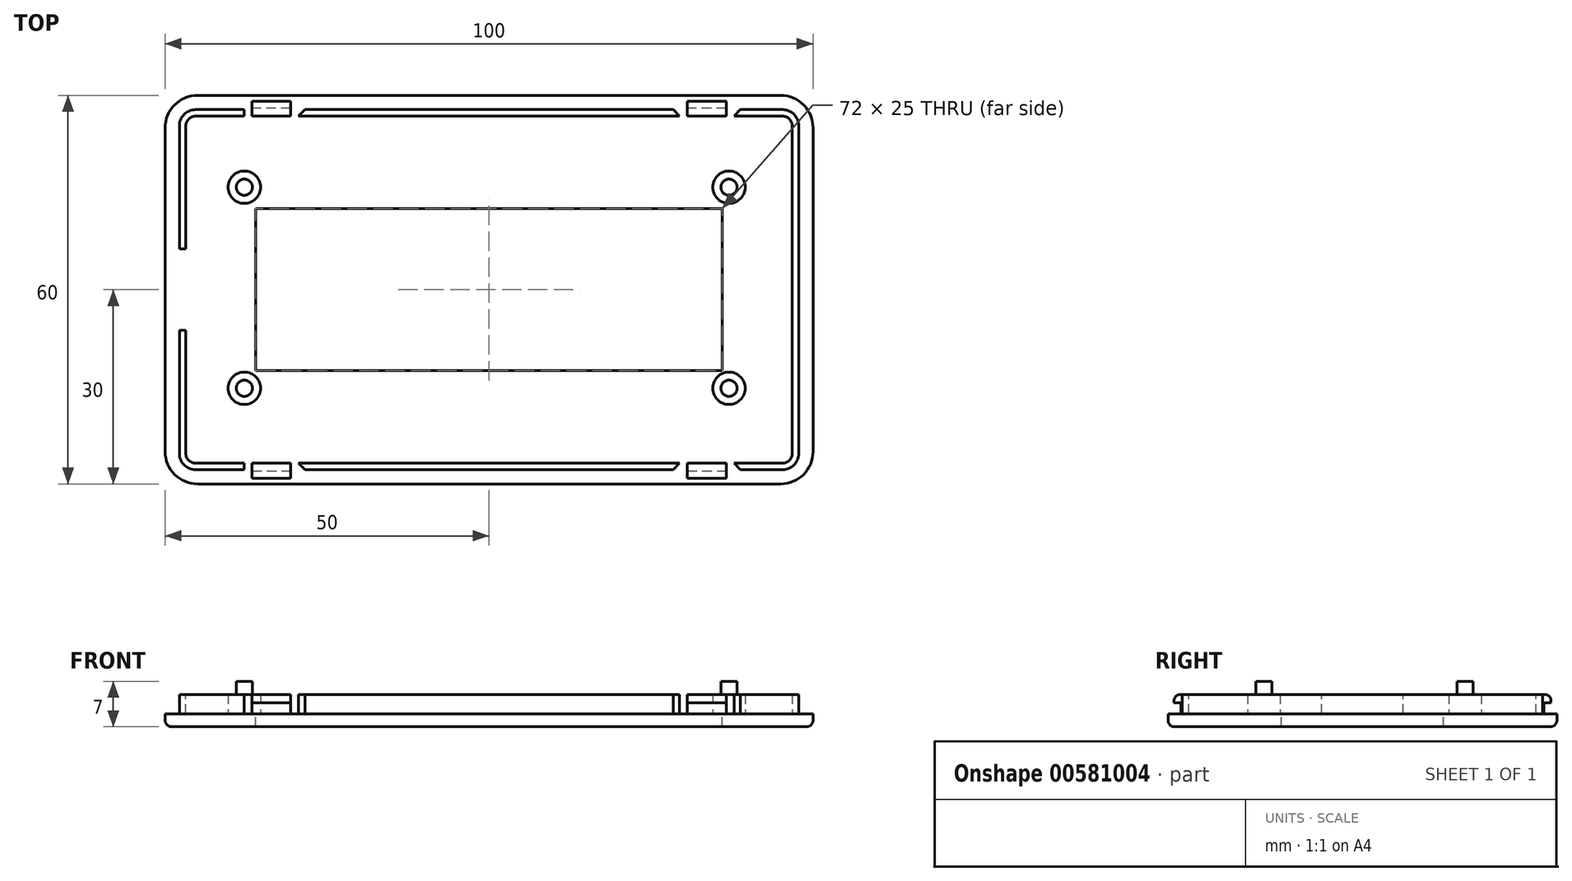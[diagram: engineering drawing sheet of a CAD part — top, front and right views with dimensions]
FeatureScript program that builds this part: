
annotation { "Feature Type Name" : "Feature", "Feature Type Description" : "" }
export const myFeature = defineFeature(function(context is Context, id is Id, definition is map)
    precondition{}
    {
        {
            var Q0;
            Q0=qCreatedBy(makeId("Top.planeOp"),FACE);
            var sketch = newSketch(context, id + "F0", { "sketchPlane" : qUnion([Q0])});
            skLineSegment(sketch, "E0.bottom", {"start": v(5, 0) * mm, "end": v(95, 0) * mm});
            skLineSegment(sketch, "E0.left", {"start": v(0, 5) * mm, "end": v(0, 30) * mm});
            skLineSegment(sketch, "E0.right", {"start": v(100, 5) * mm, "end": v(100, 30) * mm});
            skLineSegment(sketch, "E1.top", {"start": v(4.7, 2.2) * mm, "end": v(95.3, 2.2) * mm});
            skLineSegment(sketch, "E1.left", {"start": v(2.2, 30) * mm, "end": v(2.2, 4.7) * mm});
            skLineSegment(sketch, "E1.right", {"start": v(97.8, 30) * mm, "end": v(97.8, 4.7) * mm});
            skPoint(sketch, "E2.visualSharp", {"position": v(0, 0) * mm});
            skArc(sketch, "E2.filletArc", {"start": v(0, 5) * mm, "mid": v(1.46, 1.46) * mm, "end": v(5, 0) * mm});
            skPoint(sketch, "E3.visualSharp", {"position": v(100, 0) * mm});
            skArc(sketch, "E3.filletArc", {"start": v(95, 0) * mm, "mid": v(98.54, 1.46) * mm, "end": v(100, 5) * mm});
            skPoint(sketch, "E4.visualSharp", {"position": v(97.8, 2.2) * mm});
            skArc(sketch, "E4.filletArc", {"start": v(95.3, 2.2) * mm, "mid": v(97.07, 2.93) * mm, "end": v(97.8, 4.7) * mm});
            skPoint(sketch, "E5.visualSharp", {"position": v(2.2, 2.2) * mm});
            skArc(sketch, "E5.filletArc", {"start": v(2.2, 4.7) * mm, "mid": v(2.93, 2.93) * mm, "end": v(4.7, 2.2) * mm});
            skLineSegment(sketch, "E6.1", {"start": v(3.2, 30) * mm, "end": v(3.2, 4.7) * mm});
            skLineSegment(sketch, "E6.2", {"start": v(4.7, 3.2) * mm, "end": v(95.3, 3.2) * mm});
            skLineSegment(sketch, "E6.3", {"start": v(96.8, 30) * mm, "end": v(96.8, 4.7) * mm});
            skPoint(sketch, "E7.visualSharp", {"position": v(96.8, 3.2) * mm});
            skArc(sketch, "E7.filletArc", {"start": v(95.3, 3.2) * mm, "mid": v(96.36, 3.64) * mm, "end": v(96.8, 4.7) * mm});
            skPoint(sketch, "E8.visualSharp", {"position": v(3.2, 3.2) * mm});
            skArc(sketch, "E8.filletArc", {"start": v(3.2, 4.7) * mm, "mid": v(3.64, 3.64) * mm, "end": v(4.7, 3.2) * mm});
            skLineSegment(sketch, "E9", {"start": v(0, 30) * mm, "end": v(100, 30) * mm});
            skSolve(sketch);
        }
        {
            var Q0;
            Q0=qSketchRegion(id+"F0",true);
            var Q1;
            Q1=makeQuery(id+"F0.imprint","IMPRINT",FACE,{"disambiguationData":[TD([[makeQuery(id+"F0.imprint","IMPRINT",EDGE,{"derivedFrom":sQuery(id+"F0.wireOp",EDGE,"E6.0")}),-1.0]])]});
            var Q2;
            Q2=makeQuery(id+"F0.imprint","IMPRINT",FACE,{"disambiguationData":[TD([[makeQuery(id+"F0.imprint","IMPRINT",EDGE,{"derivedFrom":sQuery(id+"F0.wireOp",EDGE,"E1.bottom")}),-1.0]])]});
            extrude(context, id + "F1", {"entities" : qUnion([Q0, Q1, Q2]), "depth" : 2 * mm, "offsetDistance" : 25 * mm});
        }
        {
            var Q0;
            Q0=makeQuery(id+"F0.imprint","IMPRINT",FACE,{"disambiguationData":[TD([[makeQuery(id+"F0.imprint","IMPRINT",EDGE,{"derivedFrom":sQuery(id+"F0.wireOp",EDGE,"E1.top")}),1.0]])]});
            extrude(context, id + "F2", {"entities" : qUnion([Q0]), "operationType" : NewBodyOperationType.ADD, "depth" : 5 * mm, "offsetDistance" : 25 * mm});
        }
        {
            var Q0;
            Q0=makeQuery(id+"F2.opExtrude","CAP_FACE",FACE,{"disambiguationData":[OSD([sQuery(id+"F0.wireOp",EDGE,"E1.top"),sQuery(id+"F0.wireOp",EDGE,"E1.left"),sQuery(id+"F0.wireOp",EDGE,"E1.right"),sQuery(id+"F0.wireOp",EDGE,"E4.filletArc"),sQuery(id+"F0.wireOp",EDGE,"E5.filletArc"),sQuery(id+"F0.wireOp",EDGE,"E6.1"),sQuery(id+"F0.wireOp",EDGE,"E6.2"),sQuery(id+"F0.wireOp",EDGE,"E6.3"),sQuery(id+"F0.wireOp",EDGE,"E7.filletArc"),sQuery(id+"F0.wireOp",EDGE,"E8.filletArc"),sQuery(id+"F0.wireOp",EDGE,"E9")])],"isStart":false});
            var sketch = newSketch(context, id + "F3", { "sketchPlane" : qUnion([Q0])});
            skLineSegment(sketch, "E10.bottom", {"start": v(2.2, 30) * mm, "end": v(3.2, 30) * mm});
            skLineSegment(sketch, "E10.top", {"start": v(2.2, 23.7) * mm, "end": v(3.2, 23.7) * mm});
            skLineSegment(sketch, "E10.left", {"start": v(2.2, 30) * mm, "end": v(2.2, 23.7) * mm});
            skLineSegment(sketch, "E10.right", {"start": v(3.2, 30) * mm, "end": v(3.2, 23.7) * mm});
            skLineSegment(sketch, "E11.bottom", {"start": v(12.2, 3.2) * mm, "end": v(13.4, 3.2) * mm});
            skLineSegment(sketch, "E11.top", {"start": v(12.2, 2.2) * mm, "end": v(13.4, 2.2) * mm});
            skLineSegment(sketch, "E11.left", {"start": v(12.2, 3.2) * mm, "end": v(12.2, 2.2) * mm});
            skLineSegment(sketch, "E11.right", {"start": v(13.4, 3.2) * mm, "end": v(13.4, 2.2) * mm});
            skLineSegment(sketch, "E12.bottom", {"start": v(86.6, 3.2) * mm, "end": v(87.8, 3.2) * mm});
            skLineSegment(sketch, "E12.top", {"start": v(86.6, 2.2) * mm, "end": v(87.8, 2.2) * mm});
            skLineSegment(sketch, "E12.left", {"start": v(86.6, 3.2) * mm, "end": v(86.6, 2.2) * mm});
            skLineSegment(sketch, "E12.right", {"start": v(87.8, 3.2) * mm, "end": v(87.8, 2.2) * mm});
            skLineSegment(sketch, "E13.bottom", {"start": v(19.4, 3.2) * mm, "end": v(20.6, 3.2) * mm});
            skLineSegment(sketch, "E13.top", {"start": v(19.4, 2.2) * mm, "end": v(20.6, 2.2) * mm});
            skLineSegment(sketch, "E13.left", {"start": v(19.4, 3.2) * mm, "end": v(19.4, 2.2) * mm});
            skLineSegment(sketch, "E13.right", {"start": v(20.6, 3.2) * mm, "end": v(20.6, 2.2) * mm});
            skLineSegment(sketch, "E14.bottom", {"start": v(80.6, 3.2) * mm, "end": v(79.4, 3.2) * mm});
            skLineSegment(sketch, "E14.top", {"start": v(80.6, 2.2) * mm, "end": v(79.4, 2.2) * mm});
            skLineSegment(sketch, "E14.left", {"start": v(80.6, 3.2) * mm, "end": v(80.6, 2.2) * mm});
            skLineSegment(sketch, "E14.right", {"start": v(79.4, 3.2) * mm, "end": v(79.4, 2.2) * mm});
            skSolve(sketch);
        }
        {
            var Q0;
            Q0=makeQuery(id+"F3.imprint","IMPRINT",FACE,{"disambiguationData":[TD([[makeQuery(id+"F3.imprint","IMPRINT",EDGE,{"derivedFrom":sQuery(id+"F3.wireOp",EDGE,"E10.bottom")}),-1.0]])]});
            var Q1;
            Q1=makeQuery(id+"F3.imprint","IMPRINT",FACE,{"disambiguationData":[TD([[makeQuery(id+"F3.imprint","IMPRINT",EDGE,{"derivedFrom":sQuery(id+"F3.wireOp",EDGE,"E11.bottom")}),-1.0]])]});
            var Q2;
            Q2=makeQuery(id+"F3.imprint","IMPRINT",FACE,{"disambiguationData":[TD([[makeQuery(id+"F3.imprint","IMPRINT",EDGE,{"derivedFrom":sQuery(id+"F3.wireOp",EDGE,"E13.bottom")}),-1.0]])]});
            var Q3;
            Q3=makeQuery(id+"F3.imprint","IMPRINT",FACE,{"disambiguationData":[TD([[makeQuery(id+"F3.imprint","IMPRINT",EDGE,{"derivedFrom":sQuery(id+"F3.wireOp",EDGE,"E14.bottom")}),-1.0]])]});
            var Q4;
            Q4=makeQuery(id+"F3.imprint","IMPRINT",FACE,{"disambiguationData":[TD([[makeQuery(id+"F3.imprint","IMPRINT",EDGE,{"derivedFrom":sQuery(id+"F3.wireOp",EDGE,"E12.bottom")}),-1.0]])]});
            extrude(context, id + "F4", {"entities" : qUnion([Q0, Q1, Q2, Q3, Q4]), "operationType" : NewBodyOperationType.REMOVE, "oppositeDirection" : true, "depth" : 3 * mm, "offsetDistance" : 25 * mm});
        }
        {
            var Q0;
            {var subQ0=sQuery(id+"F3.wireOp",EDGE,"E11.right");var subQ2=sQuery(id+"F0.wireOp",EDGE,"E1.top");Q0=makeQuery(id+"F4.boolean.opBoolean","SPLIT",FACE,{"disambiguationData":[TD([makeQuery(id+"F4.opExtrude","SWEPT_FACE",FACE,{"disambiguationData":[OSD([subQ0])]})])],"derivedFrom":makeQuery(id+"F2.opExtrude","SWEPT_FACE",FACE,{"disambiguationData":[OSD([subQ2])]})});}
            var Q1;
            {var subQ1=sQuery(id+"F0.wireOp",EDGE,"E1.top");var subQ3=sQuery(id+"F3.wireOp",EDGE,"E12.left");Q1=makeQuery(id+"F4.boolean.opBoolean","SPLIT",FACE,{"disambiguationData":[TD([makeQuery(id+"F4.opExtrude","SWEPT_FACE",FACE,{"disambiguationData":[OSD([subQ3])]})])],"derivedFrom":makeQuery(id+"F2.opExtrude","SWEPT_FACE",FACE,{"disambiguationData":[OSD([subQ1])]})});}
            extrude(context, id + "F5", {"entities" : qUnion([Q0, Q1]), "operationType" : NewBodyOperationType.ADD, "depth" : 0.2 * mm, "offsetDistance" : 25 * mm});
        }
        {
            var Q0;
            {var subQ0=sQuery(id+"F3.wireOp",EDGE,"E11.right");var subQ2=sQuery(id+"F0.wireOp",EDGE,"E1.top");Q0=makeQuery(id+"F5.opExtrude","CAP_FACE",FACE,{"disambiguationData":[OSD([subQ2]),TDD([makeQuery(id+"F4.boolean.opBoolean","SPLIT",FACE,{"disambiguationData":[TD([makeQuery(id+"F4.opExtrude","SWEPT_FACE",FACE,{"disambiguationData":[OSD([subQ0])]})])],"derivedFrom":makeQuery(id+"F2.opExtrude","SWEPT_FACE",FACE,{"disambiguationData":[OSD([subQ2])]})})])],"isStart":false});}
            var sketch = newSketch(context, id + "F6", { "sketchPlane" : qUnion([Q0])});
            skLineSegment(sketch, "E15.bottom", {"start": v(13.4, 5) * mm, "end": v(19.4, 5) * mm});
            skLineSegment(sketch, "E15.top", {"start": v(13.4, 3.7) * mm, "end": v(19.4, 3.7) * mm});
            skLineSegment(sketch, "E15.left", {"start": v(13.4, 5) * mm, "end": v(13.4, 3.7) * mm});
            skLineSegment(sketch, "E15.right", {"start": v(19.4, 5) * mm, "end": v(19.4, 3.7) * mm});
            skSolve(sketch);
        }
        {
            var Q0;
            {var subQ1=sQuery(id+"F0.wireOp",EDGE,"E1.top");var subQ3=sQuery(id+"F3.wireOp",EDGE,"E12.left");Q0=makeQuery(id+"F5.opExtrude","CAP_FACE",FACE,{"disambiguationData":[OSD([subQ1]),TDD([makeQuery(id+"F4.boolean.opBoolean","SPLIT",FACE,{"disambiguationData":[TD([makeQuery(id+"F4.opExtrude","SWEPT_FACE",FACE,{"disambiguationData":[OSD([subQ3])]})])],"derivedFrom":makeQuery(id+"F2.opExtrude","SWEPT_FACE",FACE,{"disambiguationData":[OSD([subQ1])]})})])],"isStart":false});}
            var sketch = newSketch(context, id + "F7", { "sketchPlane" : qUnion([Q0])});
            skLineSegment(sketch, "E16.bottom", {"start": v(80.6, 5) * mm, "end": v(86.6, 5) * mm});
            skLineSegment(sketch, "E16.top", {"start": v(80.6, 3.7) * mm, "end": v(86.6, 3.7) * mm});
            skLineSegment(sketch, "E16.left", {"start": v(80.6, 5) * mm, "end": v(80.6, 3.7) * mm});
            skLineSegment(sketch, "E16.right", {"start": v(86.6, 5) * mm, "end": v(86.6, 3.7) * mm});
            skSolve(sketch);
        }
        {
            var Q0;
            Q0=makeQuery(id+"F6.imprint","IMPRINT",FACE,{"disambiguationData":[TD([[makeQuery(id+"F6.imprint","IMPRINT",EDGE,{"derivedFrom":sQuery(id+"F6.wireOp",EDGE,"E15.bottom")}),-1.0]])]});
            var Q1;
            Q1=makeQuery(id+"F7.imprint","IMPRINT",FACE,{"disambiguationData":[TD([[makeQuery(id+"F7.imprint","IMPRINT",EDGE,{"derivedFrom":sQuery(id+"F7.wireOp",EDGE,"E16.bottom")}),-1.0]])]});
            extrude(context, id + "F8", {"entities" : qUnion([Q0, Q1]), "operationType" : NewBodyOperationType.ADD, "depth" : 1.1 * mm, "offsetDistance" : 25 * mm});
        }
        {
            var Q0;
            Q0=makeQuery(id+"F8.opExtrude","CAP_EDGE",EDGE,{"disambiguationData":[OSD([sQuery(id+"F6.wireOp",EDGE,"E15.bottom")])],"isStart":false});
            var Q1;
            Q1=makeQuery(id+"F8.opExtrude","CAP_EDGE",EDGE,{"disambiguationData":[OSD([sQuery(id+"F7.wireOp",EDGE,"E16.bottom")])],"isStart":false});
            fillet(context, id + "F9", {"entities" : qUnion([Q0, Q1]), "radius" : 1 * mm, "tangentPropagation" : true, "allowEdgeOverflow" : false});
        }
        {
            var Q0;
            Q0=makeQuery(id+"F4.boolean.opBoolean","COPY",EDGE,{"derivedFrom":makeQuery(id+"F4.opExtrude","SWEPT_EDGE",EDGE,{"disambiguationData":[OSD([sQuery(id+"F0.wireOp",EDGE,"E1.top"),sQuery(id+"F3.wireOp",EDGE,"E13.top"),sQuery(id+"F3.wireOp",EDGE,"E13.right")])]})});
            var Q1;
            Q1=makeQuery(id+"F4.boolean.opBoolean","COPY",EDGE,{"derivedFrom":makeQuery(id+"F4.opExtrude","SWEPT_EDGE",EDGE,{"disambiguationData":[OSD([sQuery(id+"F0.wireOp",EDGE,"E1.top"),sQuery(id+"F3.wireOp",EDGE,"E11.top"),sQuery(id+"F3.wireOp",EDGE,"E11.left")])]})});
            var Q2;
            Q2=makeQuery(id+"F4.boolean.opBoolean","COPY",EDGE,{"derivedFrom":makeQuery(id+"F4.opExtrude","SWEPT_EDGE",EDGE,{"disambiguationData":[OSD([sQuery(id+"F0.wireOp",EDGE,"E1.top"),sQuery(id+"F3.wireOp",EDGE,"E14.top"),sQuery(id+"F3.wireOp",EDGE,"E14.right")])]})});
            var Q3;
            Q3=makeQuery(id+"F4.boolean.opBoolean","COPY",EDGE,{"derivedFrom":makeQuery(id+"F4.opExtrude","SWEPT_EDGE",EDGE,{"disambiguationData":[OSD([sQuery(id+"F0.wireOp",EDGE,"E1.top"),sQuery(id+"F3.wireOp",EDGE,"E12.top"),sQuery(id+"F3.wireOp",EDGE,"E12.right")])]})});
            var Q4;
            Q4=makeQuery(id+"F4.boolean.opBoolean","COPY",EDGE,{"derivedFrom":makeQuery(id+"F4.opExtrude","SWEPT_EDGE",EDGE,{"disambiguationData":[OSD([sQuery(id+"F0.wireOp",EDGE,"E1.left"),sQuery(id+"F3.wireOp",EDGE,"E10.top"),sQuery(id+"F3.wireOp",EDGE,"E10.left")])]})});
            chamfer(context, id + "F10", {"entities" : qUnion([Q0, Q1, Q2, Q3, Q4]), "width" : 1 * mm, "tangentPropagation" : true});
        }
        {
            var Q0;
            {var subQ2=sQuery(id+"F0.wireOp",EDGE,"E9");var subQ4=sQuery(id+"F0.wireOp",EDGE,"E3.filletArc");var subQ5=sQuery(id+"F0.wireOp",EDGE,"E0.bottom");var subQ6=sQuery(id+"F0.wireOp",EDGE,"E2.filletArc");var subQ7=sQuery(id+"F0.wireOp",EDGE,"E0.left");var subQ8=sQuery(id+"F0.wireOp",EDGE,"E0.right");var subQ9=sQuery(id+"F0.wireOp",EDGE,"E6.1");var subQ13=makeQuery(id+"F1.opExtrude","CAP_FACE",FACE,{"disambiguationData":[OSD([subQ5,subQ7,subQ8,subQ6,subQ4,subQ2])],"isStart":false});Q0=makeQuery(id+"F4.boolean.opBoolean","MERGE",FACE,{"derivedFrom":[makeQuery(id+"F2.boolean.opBoolean","SPLIT",FACE,{"disambiguationData":[TD([makeQuery(id+"F2.opExtrude","SWEPT_FACE",FACE,{"disambiguationData":[OSD([subQ9])]})])],"derivedFrom":subQ13}),makeQuery(id+"F2.boolean.opBoolean","SPLIT",FACE,{"disambiguationData":[TD([makeQuery(id+"F1.opExtrude","SWEPT_FACE",FACE,{"disambiguationData":[OSD([subQ5])]})])],"derivedFrom":subQ13}),makeQuery(id+"F4.opExtrude","CAP_FACE",FACE,{"disambiguationData":[OSD([sQuery(id+"F3.wireOp",EDGE,"E10.bottom"),sQuery(id+"F3.wireOp",EDGE,"E10.top"),sQuery(id+"F3.wireOp",EDGE,"E10.left"),sQuery(id+"F3.wireOp",EDGE,"E10.right")])],"isStart":false}),makeQuery(id+"F4.opExtrude","CAP_FACE",FACE,{"disambiguationData":[OSD([sQuery(id+"F3.wireOp",EDGE,"E11.bottom"),sQuery(id+"F3.wireOp",EDGE,"E11.top"),sQuery(id+"F3.wireOp",EDGE,"E11.left"),sQuery(id+"F3.wireOp",EDGE,"E11.right")])],"isStart":false}),makeQuery(id+"F4.opExtrude","CAP_FACE",FACE,{"disambiguationData":[OSD([sQuery(id+"F3.wireOp",EDGE,"E12.bottom"),sQuery(id+"F3.wireOp",EDGE,"E12.top"),sQuery(id+"F3.wireOp",EDGE,"E12.left"),sQuery(id+"F3.wireOp",EDGE,"E12.right")])],"isStart":false}),makeQuery(id+"F4.opExtrude","CAP_FACE",FACE,{"disambiguationData":[OSD([sQuery(id+"F3.wireOp",EDGE,"E13.bottom"),sQuery(id+"F3.wireOp",EDGE,"E13.top"),sQuery(id+"F3.wireOp",EDGE,"E13.left"),sQuery(id+"F3.wireOp",EDGE,"E13.right")])],"isStart":false}),makeQuery(id+"F4.opExtrude","CAP_FACE",FACE,{"disambiguationData":[OSD([sQuery(id+"F3.wireOp",EDGE,"E14.bottom"),sQuery(id+"F3.wireOp",EDGE,"E14.top"),sQuery(id+"F3.wireOp",EDGE,"E14.left"),sQuery(id+"F3.wireOp",EDGE,"E14.right")])],"isStart":false})]});}
            var sketch = newSketch(context, id + "F11", { "sketchPlane" : qUnion([Q0])});
            skLineSegment(sketch, "E17.bottom", {"start": v(86, 17.5) * mm, "end": v(14, 17.5) * mm});
            skLineSegment(sketch, "E17.top", {"start": v(86, 42.5) * mm, "end": v(14, 42.5) * mm});
            skLineSegment(sketch, "E17.left", {"start": v(86, 17.5) * mm, "end": v(86, 42.5) * mm});
            skLineSegment(sketch, "E17.right", {"start": v(14, 17.5) * mm, "end": v(14, 42.5) * mm});
            skPoint(sketch, "E17.middle", {"position": v(50, 30) * mm});
            skSolve(sketch);
        }
        {
            var Q0;
            {var subQ0=sQuery(id+"F11.wireOp",EDGE,"E17.bottom");Q0=makeQuery(id+"F11.imprint","IMPRINT",FACE,{"disambiguationData":[TD([[makeQuery(id+"F11.imprint","IMPRINT",EDGE,{"derivedFrom":subQ0}),-1.0]])]});}
            extrude(context, id + "F12", {"entities" : qUnion([Q0]), "operationType" : NewBodyOperationType.REMOVE, "endBound" : BoundingType.UP_TO_NEXT, "oppositeDirection" : true, "depth" : 25 * mm, "offsetDistance" : 25 * mm});
        }
        {
            var Q0;
            Q0=makeQuery(id+"F1.opExtrude","CAP_EDGE",EDGE,{"disambiguationData":[OSD([sQuery(id+"F0.wireOp",EDGE,"E0.bottom")])],"isStart":true});
            fillet(context, id + "F13", {"entities" : qUnion([Q0]), "radius" : 1 * mm, "tangentPropagation" : true, "allowEdgeOverflow" : false});
        }
        {
            var Q0;
            Q0=makeQuery(id+"F1.opExtrude","SWEPT_BODY",BODY,{"disambiguationData":[OSD([sQuery(id+"F0.wireOp",EDGE,"E0.bottom"),sQuery(id+"F0.wireOp",EDGE,"E0.left"),sQuery(id+"F0.wireOp",EDGE,"E0.right"),sQuery(id+"F0.wireOp",EDGE,"E2.filletArc"),sQuery(id+"F0.wireOp",EDGE,"E3.filletArc"),sQuery(id+"F0.wireOp",EDGE,"E9")])]});
            var Q1;
            {var subQ0=sQuery(id+"F0.wireOp",EDGE,"E0.left");var subQ1=sQuery(id+"F0.wireOp",EDGE,"E9");Q1=makeQuery(id+"F12.boolean.opBoolean","SPLIT",FACE,{"disambiguationData":[TD([makeQuery(id+"F1.opExtrude","SWEPT_FACE",FACE,{"disambiguationData":[OSD([subQ0])]})])],"derivedFrom":makeQuery(id+"F2.boolean.opBoolean","MERGE",FACE,{"derivedFrom":[makeQuery(id+"F1.opExtrude","SWEPT_FACE",FACE,{"disambiguationData":[OSD([subQ1])]}),makeQuery(id+"F2.opExtrude","SWEPT_FACE",FACE,{"disambiguationData":[OSD([subQ1]),TDD([makeQuery(id+"F0.imprint","IMPRINT",EDGE,{"disambiguationData":[TD([[makeQuery(id+"F0.imprint","INTERSECT",VERTEX,{"derivedFrom":[sQuery(id+"F0.wireOp",EDGE,"E1.left"),subQ1]}),-1.0]])],"derivedFrom":subQ1})])]}),makeQuery(id+"F2.opExtrude","SWEPT_FACE",FACE,{"disambiguationData":[OSD([subQ1]),TDD([makeQuery(id+"F0.imprint","IMPRINT",EDGE,{"disambiguationData":[TD([[makeQuery(id+"F0.imprint","INTERSECT",VERTEX,{"derivedFrom":[sQuery(id+"F0.wireOp",EDGE,"E1.right"),subQ1]}),1.0]])],"derivedFrom":subQ1})])]})]})});}
            mirror(context, id + "F14", {"operationType" : NewBodyOperationType.ADD, "entities" : qUnion([Q0]), "mirrorPlane" : qUnion([Q1])});
        }
        {
            var Q0;
            {var subQ2=sQuery(id+"F0.wireOp",EDGE,"E9");var subQ4=sQuery(id+"F0.wireOp",EDGE,"E3.filletArc");var subQ5=sQuery(id+"F0.wireOp",EDGE,"E0.bottom");var subQ6=sQuery(id+"F0.wireOp",EDGE,"E2.filletArc");var subQ7=sQuery(id+"F0.wireOp",EDGE,"E0.left");var subQ8=sQuery(id+"F0.wireOp",EDGE,"E0.right");var subQ9=sQuery(id+"F0.wireOp",EDGE,"E6.1");var subQ13=makeQuery(id+"F1.opExtrude","CAP_FACE",FACE,{"disambiguationData":[OSD([subQ5,subQ7,subQ8,subQ6,subQ4,subQ2])],"isStart":false});var subQ14=makeQuery(id+"F4.boolean.opBoolean","MERGE",FACE,{"derivedFrom":[makeQuery(id+"F2.boolean.opBoolean","SPLIT",FACE,{"disambiguationData":[TD([makeQuery(id+"F2.opExtrude","SWEPT_FACE",FACE,{"disambiguationData":[OSD([subQ9])]})])],"derivedFrom":subQ13}),makeQuery(id+"F2.boolean.opBoolean","SPLIT",FACE,{"disambiguationData":[TD([makeQuery(id+"F1.opExtrude","SWEPT_FACE",FACE,{"disambiguationData":[OSD([subQ5])]})])],"derivedFrom":subQ13}),makeQuery(id+"F4.opExtrude","CAP_FACE",FACE,{"disambiguationData":[OSD([sQuery(id+"F3.wireOp",EDGE,"E10.bottom"),sQuery(id+"F3.wireOp",EDGE,"E10.top"),sQuery(id+"F3.wireOp",EDGE,"E10.left"),sQuery(id+"F3.wireOp",EDGE,"E10.right")])],"isStart":false}),makeQuery(id+"F4.opExtrude","CAP_FACE",FACE,{"disambiguationData":[OSD([sQuery(id+"F3.wireOp",EDGE,"E11.bottom"),sQuery(id+"F3.wireOp",EDGE,"E11.top"),sQuery(id+"F3.wireOp",EDGE,"E11.left"),sQuery(id+"F3.wireOp",EDGE,"E11.right")])],"isStart":false}),makeQuery(id+"F4.opExtrude","CAP_FACE",FACE,{"disambiguationData":[OSD([sQuery(id+"F3.wireOp",EDGE,"E12.bottom"),sQuery(id+"F3.wireOp",EDGE,"E12.top"),sQuery(id+"F3.wireOp",EDGE,"E12.left"),sQuery(id+"F3.wireOp",EDGE,"E12.right")])],"isStart":false}),makeQuery(id+"F4.opExtrude","CAP_FACE",FACE,{"disambiguationData":[OSD([sQuery(id+"F3.wireOp",EDGE,"E13.bottom"),sQuery(id+"F3.wireOp",EDGE,"E13.top"),sQuery(id+"F3.wireOp",EDGE,"E13.left"),sQuery(id+"F3.wireOp",EDGE,"E13.right")])],"isStart":false}),makeQuery(id+"F4.opExtrude","CAP_FACE",FACE,{"disambiguationData":[OSD([sQuery(id+"F3.wireOp",EDGE,"E14.bottom"),sQuery(id+"F3.wireOp",EDGE,"E14.top"),sQuery(id+"F3.wireOp",EDGE,"E14.left"),sQuery(id+"F3.wireOp",EDGE,"E14.right")])],"isStart":false})]});Q0=makeQuery(id+"F14.boolean.opBoolean","MERGE",FACE,{"derivedFrom":[subQ14,makeQuery(id+"F14.opPattern","COPY",FACE,{"derivedFrom":subQ14,"instanceName":"1"})]});}
            var sketch = newSketch(context, id + "F15", { "sketchPlane" : qUnion([Q0])});
            skCircle(sketch, "E18", {"center": v(12.22, 45.83) * mm, "radius": 1.25 * mm});
            skCircle(sketch, "E19", {"center": v(87.03, 45.83) * mm, "radius": 1.25 * mm});
            skCircle(sketch, "E20", {"center": v(87.03, 14.78) * mm, "radius": 1.25 * mm});
            skCircle(sketch, "E21", {"center": v(12.22, 14.78) * mm, "radius": 1.25 * mm});
            skCircle(sketch, "E22", {"center": v(12.22, 45.83) * mm, "radius": 2.5 * mm});
            skCircle(sketch, "E23", {"center": v(87.03, 45.83) * mm, "radius": 2.5 * mm});
            skCircle(sketch, "E24", {"center": v(87.03, 14.78) * mm, "radius": 2.5 * mm});
            skCircle(sketch, "E25", {"center": v(12.22, 14.78) * mm, "radius": 2.5 * mm});
            skSolve(sketch);
        }
        {
            var Q0;
            Q0=qSketchRegion(id+"F15",true);
            extrude(context, id + "F16", {"entities" : qUnion([Q0]), "operationType" : NewBodyOperationType.ADD, "depth" : 3 * mm, "offsetDistance" : 25 * mm});
        }
        {
            var Q0;
            {var subQ2=sQuery(id+"F0.wireOp",EDGE,"E9");var subQ4=sQuery(id+"F0.wireOp",EDGE,"E3.filletArc");var subQ5=sQuery(id+"F0.wireOp",EDGE,"E0.bottom");var subQ6=sQuery(id+"F0.wireOp",EDGE,"E2.filletArc");var subQ7=sQuery(id+"F0.wireOp",EDGE,"E0.left");var subQ8=sQuery(id+"F0.wireOp",EDGE,"E0.right");var subQ9=sQuery(id+"F0.wireOp",EDGE,"E6.1");var subQ13=makeQuery(id+"F1.opExtrude","CAP_FACE",FACE,{"disambiguationData":[OSD([subQ5,subQ7,subQ8,subQ6,subQ4,subQ2])],"isStart":false});var subQ14=makeQuery(id+"F4.boolean.opBoolean","MERGE",FACE,{"derivedFrom":[makeQuery(id+"F2.boolean.opBoolean","SPLIT",FACE,{"disambiguationData":[TD([makeQuery(id+"F2.opExtrude","SWEPT_FACE",FACE,{"disambiguationData":[OSD([subQ9])]})])],"derivedFrom":subQ13}),makeQuery(id+"F2.boolean.opBoolean","SPLIT",FACE,{"disambiguationData":[TD([makeQuery(id+"F1.opExtrude","SWEPT_FACE",FACE,{"disambiguationData":[OSD([subQ5])]})])],"derivedFrom":subQ13}),makeQuery(id+"F4.opExtrude","CAP_FACE",FACE,{"disambiguationData":[OSD([sQuery(id+"F3.wireOp",EDGE,"E10.bottom"),sQuery(id+"F3.wireOp",EDGE,"E10.top"),sQuery(id+"F3.wireOp",EDGE,"E10.left"),sQuery(id+"F3.wireOp",EDGE,"E10.right")])],"isStart":false}),makeQuery(id+"F4.opExtrude","CAP_FACE",FACE,{"disambiguationData":[OSD([sQuery(id+"F3.wireOp",EDGE,"E11.bottom"),sQuery(id+"F3.wireOp",EDGE,"E11.top"),sQuery(id+"F3.wireOp",EDGE,"E11.left"),sQuery(id+"F3.wireOp",EDGE,"E11.right")])],"isStart":false}),makeQuery(id+"F4.opExtrude","CAP_FACE",FACE,{"disambiguationData":[OSD([sQuery(id+"F3.wireOp",EDGE,"E12.bottom"),sQuery(id+"F3.wireOp",EDGE,"E12.top"),sQuery(id+"F3.wireOp",EDGE,"E12.left"),sQuery(id+"F3.wireOp",EDGE,"E12.right")])],"isStart":false}),makeQuery(id+"F4.opExtrude","CAP_FACE",FACE,{"disambiguationData":[OSD([sQuery(id+"F3.wireOp",EDGE,"E13.bottom"),sQuery(id+"F3.wireOp",EDGE,"E13.top"),sQuery(id+"F3.wireOp",EDGE,"E13.left"),sQuery(id+"F3.wireOp",EDGE,"E13.right")])],"isStart":false}),makeQuery(id+"F4.opExtrude","CAP_FACE",FACE,{"disambiguationData":[OSD([sQuery(id+"F3.wireOp",EDGE,"E14.bottom"),sQuery(id+"F3.wireOp",EDGE,"E14.top"),sQuery(id+"F3.wireOp",EDGE,"E14.left"),sQuery(id+"F3.wireOp",EDGE,"E14.right")])],"isStart":false})]});Q0=makeQuery(id+"F16.boolean.opBoolean","SPLIT",FACE,{"disambiguationData":[TD([makeQuery(id+"F16.opExtrude","SWEPT_FACE",FACE,{"disambiguationData":[OSD([sQuery(id+"F15.wireOp",EDGE,"E21")])]})])],"derivedFrom":makeQuery(id+"F14.boolean.opBoolean","MERGE",FACE,{"derivedFrom":[subQ14,makeQuery(id+"F14.opPattern","COPY",FACE,{"derivedFrom":subQ14,"instanceName":"1"})]})});}
            var Q1;
            {var subQ2=sQuery(id+"F0.wireOp",EDGE,"E9");var subQ4=sQuery(id+"F0.wireOp",EDGE,"E3.filletArc");var subQ5=sQuery(id+"F0.wireOp",EDGE,"E0.bottom");var subQ6=sQuery(id+"F0.wireOp",EDGE,"E2.filletArc");var subQ7=sQuery(id+"F0.wireOp",EDGE,"E0.left");var subQ8=sQuery(id+"F0.wireOp",EDGE,"E0.right");var subQ9=sQuery(id+"F0.wireOp",EDGE,"E6.1");var subQ13=makeQuery(id+"F1.opExtrude","CAP_FACE",FACE,{"disambiguationData":[OSD([subQ5,subQ7,subQ8,subQ6,subQ4,subQ2])],"isStart":false});var subQ14=makeQuery(id+"F4.boolean.opBoolean","MERGE",FACE,{"derivedFrom":[makeQuery(id+"F2.boolean.opBoolean","SPLIT",FACE,{"disambiguationData":[TD([makeQuery(id+"F2.opExtrude","SWEPT_FACE",FACE,{"disambiguationData":[OSD([subQ9])]})])],"derivedFrom":subQ13}),makeQuery(id+"F2.boolean.opBoolean","SPLIT",FACE,{"disambiguationData":[TD([makeQuery(id+"F1.opExtrude","SWEPT_FACE",FACE,{"disambiguationData":[OSD([subQ5])]})])],"derivedFrom":subQ13}),makeQuery(id+"F4.opExtrude","CAP_FACE",FACE,{"disambiguationData":[OSD([sQuery(id+"F3.wireOp",EDGE,"E10.bottom"),sQuery(id+"F3.wireOp",EDGE,"E10.top"),sQuery(id+"F3.wireOp",EDGE,"E10.left"),sQuery(id+"F3.wireOp",EDGE,"E10.right")])],"isStart":false}),makeQuery(id+"F4.opExtrude","CAP_FACE",FACE,{"disambiguationData":[OSD([sQuery(id+"F3.wireOp",EDGE,"E11.bottom"),sQuery(id+"F3.wireOp",EDGE,"E11.top"),sQuery(id+"F3.wireOp",EDGE,"E11.left"),sQuery(id+"F3.wireOp",EDGE,"E11.right")])],"isStart":false}),makeQuery(id+"F4.opExtrude","CAP_FACE",FACE,{"disambiguationData":[OSD([sQuery(id+"F3.wireOp",EDGE,"E12.bottom"),sQuery(id+"F3.wireOp",EDGE,"E12.top"),sQuery(id+"F3.wireOp",EDGE,"E12.left"),sQuery(id+"F3.wireOp",EDGE,"E12.right")])],"isStart":false}),makeQuery(id+"F4.opExtrude","CAP_FACE",FACE,{"disambiguationData":[OSD([sQuery(id+"F3.wireOp",EDGE,"E13.bottom"),sQuery(id+"F3.wireOp",EDGE,"E13.top"),sQuery(id+"F3.wireOp",EDGE,"E13.left"),sQuery(id+"F3.wireOp",EDGE,"E13.right")])],"isStart":false}),makeQuery(id+"F4.opExtrude","CAP_FACE",FACE,{"disambiguationData":[OSD([sQuery(id+"F3.wireOp",EDGE,"E14.bottom"),sQuery(id+"F3.wireOp",EDGE,"E14.top"),sQuery(id+"F3.wireOp",EDGE,"E14.left"),sQuery(id+"F3.wireOp",EDGE,"E14.right")])],"isStart":false})]});Q1=makeQuery(id+"F16.boolean.opBoolean","SPLIT",FACE,{"disambiguationData":[TD([makeQuery(id+"F16.opExtrude","SWEPT_FACE",FACE,{"disambiguationData":[OSD([sQuery(id+"F15.wireOp",EDGE,"E18")])]})])],"derivedFrom":makeQuery(id+"F14.boolean.opBoolean","MERGE",FACE,{"derivedFrom":[subQ14,makeQuery(id+"F14.opPattern","COPY",FACE,{"derivedFrom":subQ14,"instanceName":"1"})]})});}
            var Q2;
            {var subQ2=sQuery(id+"F0.wireOp",EDGE,"E9");var subQ4=sQuery(id+"F0.wireOp",EDGE,"E3.filletArc");var subQ5=sQuery(id+"F0.wireOp",EDGE,"E0.bottom");var subQ6=sQuery(id+"F0.wireOp",EDGE,"E2.filletArc");var subQ7=sQuery(id+"F0.wireOp",EDGE,"E0.left");var subQ8=sQuery(id+"F0.wireOp",EDGE,"E0.right");var subQ9=sQuery(id+"F0.wireOp",EDGE,"E6.1");var subQ13=makeQuery(id+"F1.opExtrude","CAP_FACE",FACE,{"disambiguationData":[OSD([subQ5,subQ7,subQ8,subQ6,subQ4,subQ2])],"isStart":false});var subQ14=makeQuery(id+"F4.boolean.opBoolean","MERGE",FACE,{"derivedFrom":[makeQuery(id+"F2.boolean.opBoolean","SPLIT",FACE,{"disambiguationData":[TD([makeQuery(id+"F2.opExtrude","SWEPT_FACE",FACE,{"disambiguationData":[OSD([subQ9])]})])],"derivedFrom":subQ13}),makeQuery(id+"F2.boolean.opBoolean","SPLIT",FACE,{"disambiguationData":[TD([makeQuery(id+"F1.opExtrude","SWEPT_FACE",FACE,{"disambiguationData":[OSD([subQ5])]})])],"derivedFrom":subQ13}),makeQuery(id+"F4.opExtrude","CAP_FACE",FACE,{"disambiguationData":[OSD([sQuery(id+"F3.wireOp",EDGE,"E10.bottom"),sQuery(id+"F3.wireOp",EDGE,"E10.top"),sQuery(id+"F3.wireOp",EDGE,"E10.left"),sQuery(id+"F3.wireOp",EDGE,"E10.right")])],"isStart":false}),makeQuery(id+"F4.opExtrude","CAP_FACE",FACE,{"disambiguationData":[OSD([sQuery(id+"F3.wireOp",EDGE,"E11.bottom"),sQuery(id+"F3.wireOp",EDGE,"E11.top"),sQuery(id+"F3.wireOp",EDGE,"E11.left"),sQuery(id+"F3.wireOp",EDGE,"E11.right")])],"isStart":false}),makeQuery(id+"F4.opExtrude","CAP_FACE",FACE,{"disambiguationData":[OSD([sQuery(id+"F3.wireOp",EDGE,"E12.bottom"),sQuery(id+"F3.wireOp",EDGE,"E12.top"),sQuery(id+"F3.wireOp",EDGE,"E12.left"),sQuery(id+"F3.wireOp",EDGE,"E12.right")])],"isStart":false}),makeQuery(id+"F4.opExtrude","CAP_FACE",FACE,{"disambiguationData":[OSD([sQuery(id+"F3.wireOp",EDGE,"E13.bottom"),sQuery(id+"F3.wireOp",EDGE,"E13.top"),sQuery(id+"F3.wireOp",EDGE,"E13.left"),sQuery(id+"F3.wireOp",EDGE,"E13.right")])],"isStart":false}),makeQuery(id+"F4.opExtrude","CAP_FACE",FACE,{"disambiguationData":[OSD([sQuery(id+"F3.wireOp",EDGE,"E14.bottom"),sQuery(id+"F3.wireOp",EDGE,"E14.top"),sQuery(id+"F3.wireOp",EDGE,"E14.left"),sQuery(id+"F3.wireOp",EDGE,"E14.right")])],"isStart":false})]});Q2=makeQuery(id+"F16.boolean.opBoolean","SPLIT",FACE,{"disambiguationData":[TD([makeQuery(id+"F16.opExtrude","SWEPT_FACE",FACE,{"disambiguationData":[OSD([sQuery(id+"F15.wireOp",EDGE,"E19")])]})])],"derivedFrom":makeQuery(id+"F14.boolean.opBoolean","MERGE",FACE,{"derivedFrom":[subQ14,makeQuery(id+"F14.opPattern","COPY",FACE,{"derivedFrom":subQ14,"instanceName":"1"})]})});}
            var Q3;
            {var subQ2=sQuery(id+"F0.wireOp",EDGE,"E9");var subQ4=sQuery(id+"F0.wireOp",EDGE,"E3.filletArc");var subQ5=sQuery(id+"F0.wireOp",EDGE,"E0.bottom");var subQ6=sQuery(id+"F0.wireOp",EDGE,"E2.filletArc");var subQ7=sQuery(id+"F0.wireOp",EDGE,"E0.left");var subQ8=sQuery(id+"F0.wireOp",EDGE,"E0.right");var subQ9=sQuery(id+"F0.wireOp",EDGE,"E6.1");var subQ13=makeQuery(id+"F1.opExtrude","CAP_FACE",FACE,{"disambiguationData":[OSD([subQ5,subQ7,subQ8,subQ6,subQ4,subQ2])],"isStart":false});var subQ14=makeQuery(id+"F4.boolean.opBoolean","MERGE",FACE,{"derivedFrom":[makeQuery(id+"F2.boolean.opBoolean","SPLIT",FACE,{"disambiguationData":[TD([makeQuery(id+"F2.opExtrude","SWEPT_FACE",FACE,{"disambiguationData":[OSD([subQ9])]})])],"derivedFrom":subQ13}),makeQuery(id+"F2.boolean.opBoolean","SPLIT",FACE,{"disambiguationData":[TD([makeQuery(id+"F1.opExtrude","SWEPT_FACE",FACE,{"disambiguationData":[OSD([subQ5])]})])],"derivedFrom":subQ13}),makeQuery(id+"F4.opExtrude","CAP_FACE",FACE,{"disambiguationData":[OSD([sQuery(id+"F3.wireOp",EDGE,"E10.bottom"),sQuery(id+"F3.wireOp",EDGE,"E10.top"),sQuery(id+"F3.wireOp",EDGE,"E10.left"),sQuery(id+"F3.wireOp",EDGE,"E10.right")])],"isStart":false}),makeQuery(id+"F4.opExtrude","CAP_FACE",FACE,{"disambiguationData":[OSD([sQuery(id+"F3.wireOp",EDGE,"E11.bottom"),sQuery(id+"F3.wireOp",EDGE,"E11.top"),sQuery(id+"F3.wireOp",EDGE,"E11.left"),sQuery(id+"F3.wireOp",EDGE,"E11.right")])],"isStart":false}),makeQuery(id+"F4.opExtrude","CAP_FACE",FACE,{"disambiguationData":[OSD([sQuery(id+"F3.wireOp",EDGE,"E12.bottom"),sQuery(id+"F3.wireOp",EDGE,"E12.top"),sQuery(id+"F3.wireOp",EDGE,"E12.left"),sQuery(id+"F3.wireOp",EDGE,"E12.right")])],"isStart":false}),makeQuery(id+"F4.opExtrude","CAP_FACE",FACE,{"disambiguationData":[OSD([sQuery(id+"F3.wireOp",EDGE,"E13.bottom"),sQuery(id+"F3.wireOp",EDGE,"E13.top"),sQuery(id+"F3.wireOp",EDGE,"E13.left"),sQuery(id+"F3.wireOp",EDGE,"E13.right")])],"isStart":false}),makeQuery(id+"F4.opExtrude","CAP_FACE",FACE,{"disambiguationData":[OSD([sQuery(id+"F3.wireOp",EDGE,"E14.bottom"),sQuery(id+"F3.wireOp",EDGE,"E14.top"),sQuery(id+"F3.wireOp",EDGE,"E14.left"),sQuery(id+"F3.wireOp",EDGE,"E14.right")])],"isStart":false})]});Q3=makeQuery(id+"F16.boolean.opBoolean","SPLIT",FACE,{"disambiguationData":[TD([makeQuery(id+"F16.opExtrude","SWEPT_FACE",FACE,{"disambiguationData":[OSD([sQuery(id+"F15.wireOp",EDGE,"E20")])]})])],"derivedFrom":makeQuery(id+"F14.boolean.opBoolean","MERGE",FACE,{"derivedFrom":[subQ14,makeQuery(id+"F14.opPattern","COPY",FACE,{"derivedFrom":subQ14,"instanceName":"1"})]})});}
            extrude(context, id + "F17", {"entities" : qUnion([Q0, Q1, Q2, Q3]), "operationType" : NewBodyOperationType.ADD, "depth" : 5 * mm, "offsetDistance" : 25 * mm});
        }
    });
